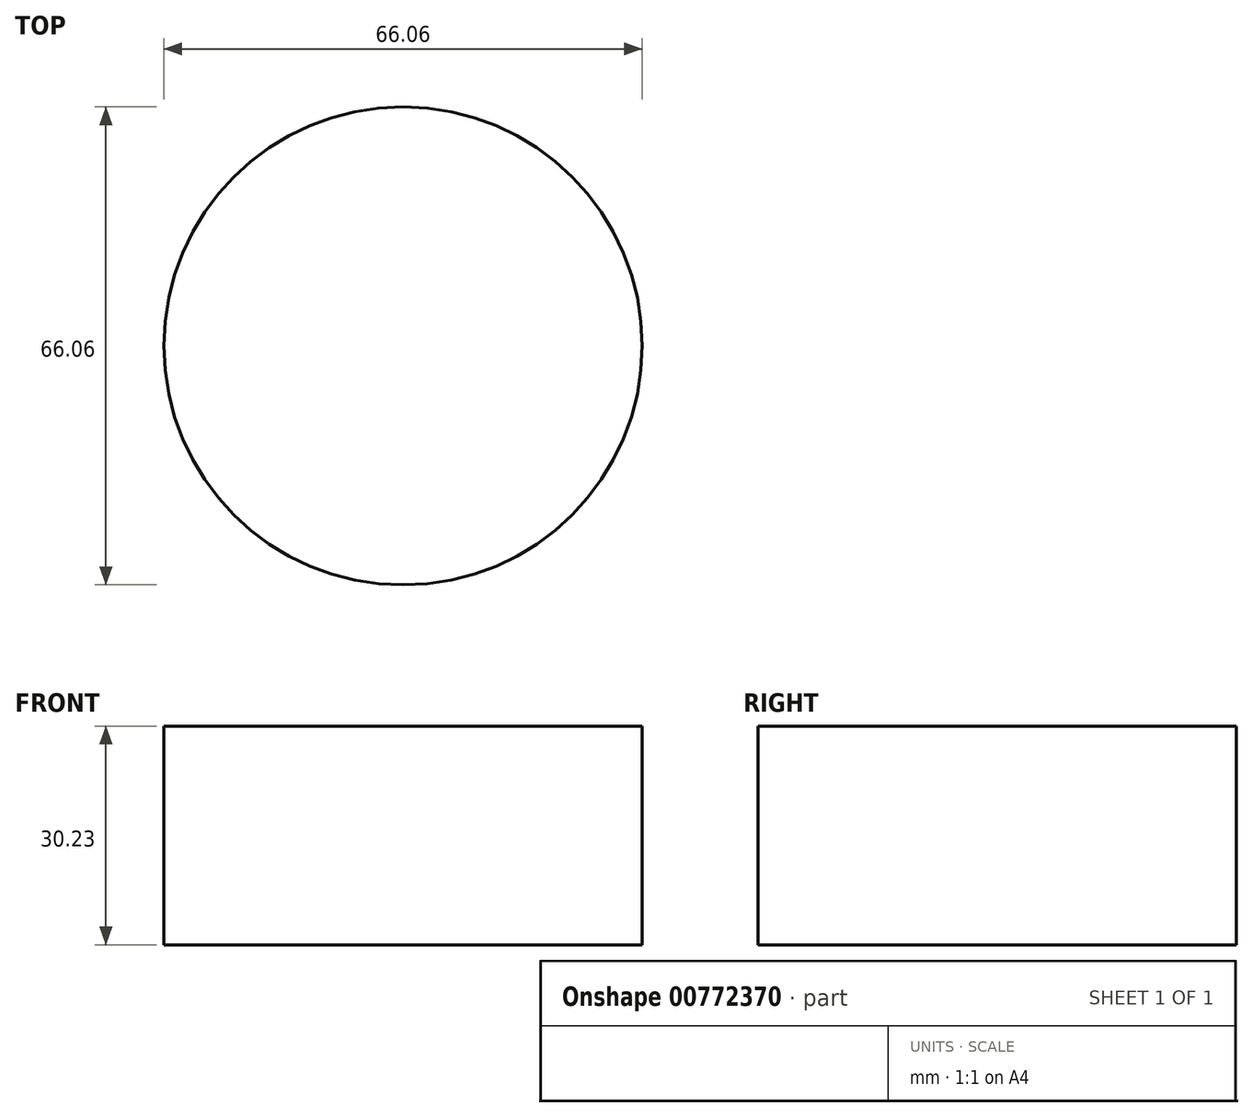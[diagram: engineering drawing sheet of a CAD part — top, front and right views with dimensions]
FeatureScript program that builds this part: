
annotation { "Feature Type Name" : "Feature", "Feature Type Description" : "" }
export const myFeature = defineFeature(function(context is Context, id is Id, definition is map)
    precondition{}
    {
        {
            var Q0;
            Q0=qCreatedBy(makeId("Top.planeOp"),FACE);
            var sketch = newSketch(context, id + "F0", { "sketchPlane" : qUnion([Q0])});
            skCircle(sketch, "E0", {"center": v(0, 0) * mm, "radius": 33.03 * mm});
            skSolve(sketch);
        }
        {
            var Q0;
            Q0 = qSketchRegion(id + "F0", true);
            extrude(context, id + "F1", {"entities" : qUnion([Q0]), "depth" : 30.23 * mm, "offsetDistance" : 25.4 * mm});
        }
    });
